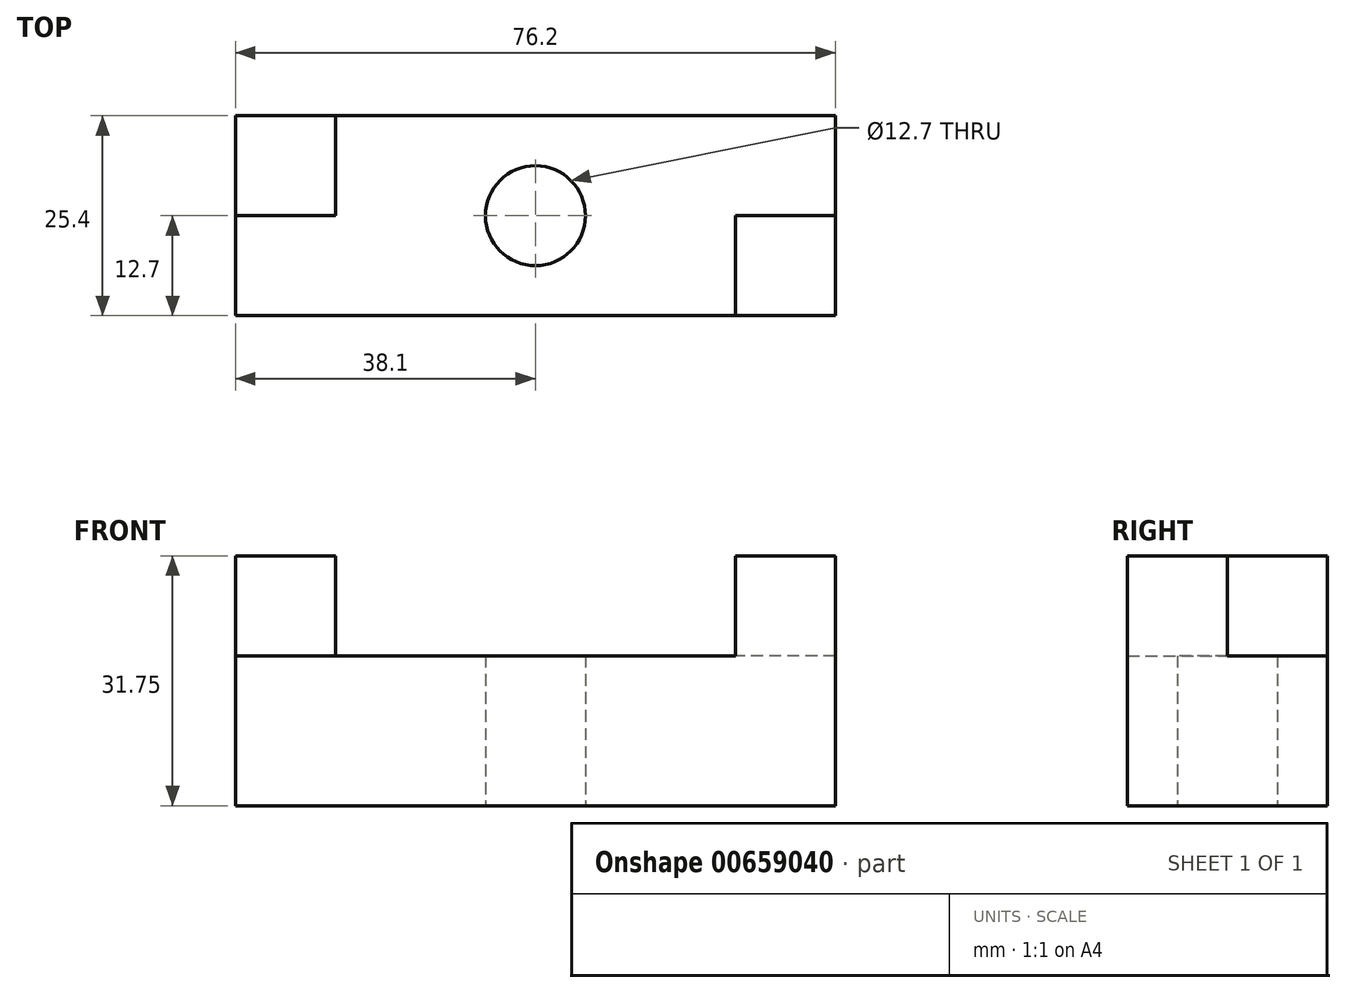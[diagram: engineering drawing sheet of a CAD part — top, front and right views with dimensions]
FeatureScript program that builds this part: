
annotation { "Feature Type Name" : "Feature", "Feature Type Description" : "" }
export const myFeature = defineFeature(function(context is Context, id is Id, definition is map)
    precondition{}
    {
        {
            var Q0;
            Q0=qCreatedBy(makeId("Top.planeOp"),FACE);
            var sketch = newSketch(context, id + "F0", { "sketchPlane" : qUnion([Q0])});
            skLineSegment(sketch, "E0.bottom", {"start": v(0, 0) * mm, "end": v(-76.2, 0) * mm});
            skLineSegment(sketch, "E0.top", {"start": v(0, 25.4) * mm, "end": v(-76.2, 25.4) * mm});
            skLineSegment(sketch, "E0.left", {"start": v(0, 0) * mm, "end": v(0, 25.4) * mm});
            skLineSegment(sketch, "E0.right", {"start": v(-76.2, 0) * mm, "end": v(-76.2, 25.4) * mm});
            skSolve(sketch);
        }
        {
            var Q0;
            Q0=makeQuery(id+"F0.imprint","IMPRINT",FACE,{"disambiguationData":[TD([[makeQuery(id+"F0.imprint","IMPRINT",EDGE,{"derivedFrom":sQuery(id+"F0.wireOp",EDGE,"E0.bottom")}),-1.0]])]});
            extrude(context, id + "F1", {"entities" : qUnion([Q0]), "depth" : 19.05 * mm, "offsetDistance" : 25.4 * mm});
        }
        {
            var Q0;
            Q0=makeQuery(id+"F1.opExtrude","CAP_FACE",FACE,{"disambiguationData":[OSD([sQuery(id+"F0.wireOp",EDGE,"E0.bottom"),sQuery(id+"F0.wireOp",EDGE,"E0.top"),sQuery(id+"F0.wireOp",EDGE,"E0.left"),sQuery(id+"F0.wireOp",EDGE,"E0.right")])],"isStart":false});
            var sketch = newSketch(context, id + "F2", { "sketchPlane" : qUnion([Q0])});
            skLineSegment(sketch, "E1.bottom", {"start": v(0, 0) * mm, "end": v(-12.7, 0) * mm});
            skLineSegment(sketch, "E1.top", {"start": v(0, 12.7) * mm, "end": v(-12.7, 12.7) * mm});
            skLineSegment(sketch, "E1.left", {"start": v(0, 0) * mm, "end": v(0, 12.7) * mm});
            skLineSegment(sketch, "E1.right", {"start": v(-12.7, 0) * mm, "end": v(-12.7, 12.7) * mm});
            skLineSegment(sketch, "E2.bottom", {"start": v(-76.2, 25.4) * mm, "end": v(-63.5, 25.4) * mm});
            skLineSegment(sketch, "E2.top", {"start": v(-76.2, 12.7) * mm, "end": v(-63.5, 12.7) * mm});
            skLineSegment(sketch, "E2.left", {"start": v(-76.2, 25.4) * mm, "end": v(-76.2, 12.7) * mm});
            skLineSegment(sketch, "E2.right", {"start": v(-63.5, 25.4) * mm, "end": v(-63.5, 12.7) * mm});
            skSolve(sketch);
        }
        {
            var Q0;
            Q0=makeQuery(id+"F2.imprint","IMPRINT",FACE,{"disambiguationData":[TD([[makeQuery(id+"F2.imprint","IMPRINT",EDGE,{"derivedFrom":sQuery(id+"F2.wireOp",EDGE,"E2.bottom")}),1.0]])]});
            var Q1;
            Q1=makeQuery(id+"F2.imprint","IMPRINT",FACE,{"disambiguationData":[TD([[makeQuery(id+"F2.imprint","IMPRINT",EDGE,{"derivedFrom":sQuery(id+"F2.wireOp",EDGE,"E1.bottom")}),-1.0]])]});
            extrude(context, id + "F3", {"entities" : qUnion([Q0, Q1]), "operationType" : NewBodyOperationType.ADD, "depth" : 12.7 * mm, "offsetDistance" : 25.4 * mm});
        }
        {
            var Q0;
            Q0=makeQuery(id+"F1.opExtrude","CAP_FACE",FACE,{"disambiguationData":[OSD([sQuery(id+"F0.wireOp",EDGE,"E0.bottom"),sQuery(id+"F0.wireOp",EDGE,"E0.top"),sQuery(id+"F0.wireOp",EDGE,"E0.left"),sQuery(id+"F0.wireOp",EDGE,"E0.right")])],"isStart":true});
            var sketch = newSketch(context, id + "F4", { "sketchPlane" : qUnion([Q0])});
            skCircle(sketch, "E3", {"center": v(-38.1, -12.7) * mm, "radius": 6.35 * mm});
            skSolve(sketch);
        }
        {
            var Q0;
            Q0=makeQuery(id+"F4.imprint","IMPRINT",FACE,{"disambiguationData":[TD([[makeQuery(id+"F4.imprint","IMPRINT",EDGE,{"derivedFrom":sQuery(id+"F4.wireOp",EDGE,"E3")}),1.0]])]});
            extrude(context, id + "F5", {"entities" : qUnion([Q0]), "operationType" : NewBodyOperationType.REMOVE, "oppositeDirection" : true, "depth" : 19.05 * mm, "offsetDistance" : 25.4 * mm});
        }
    });
